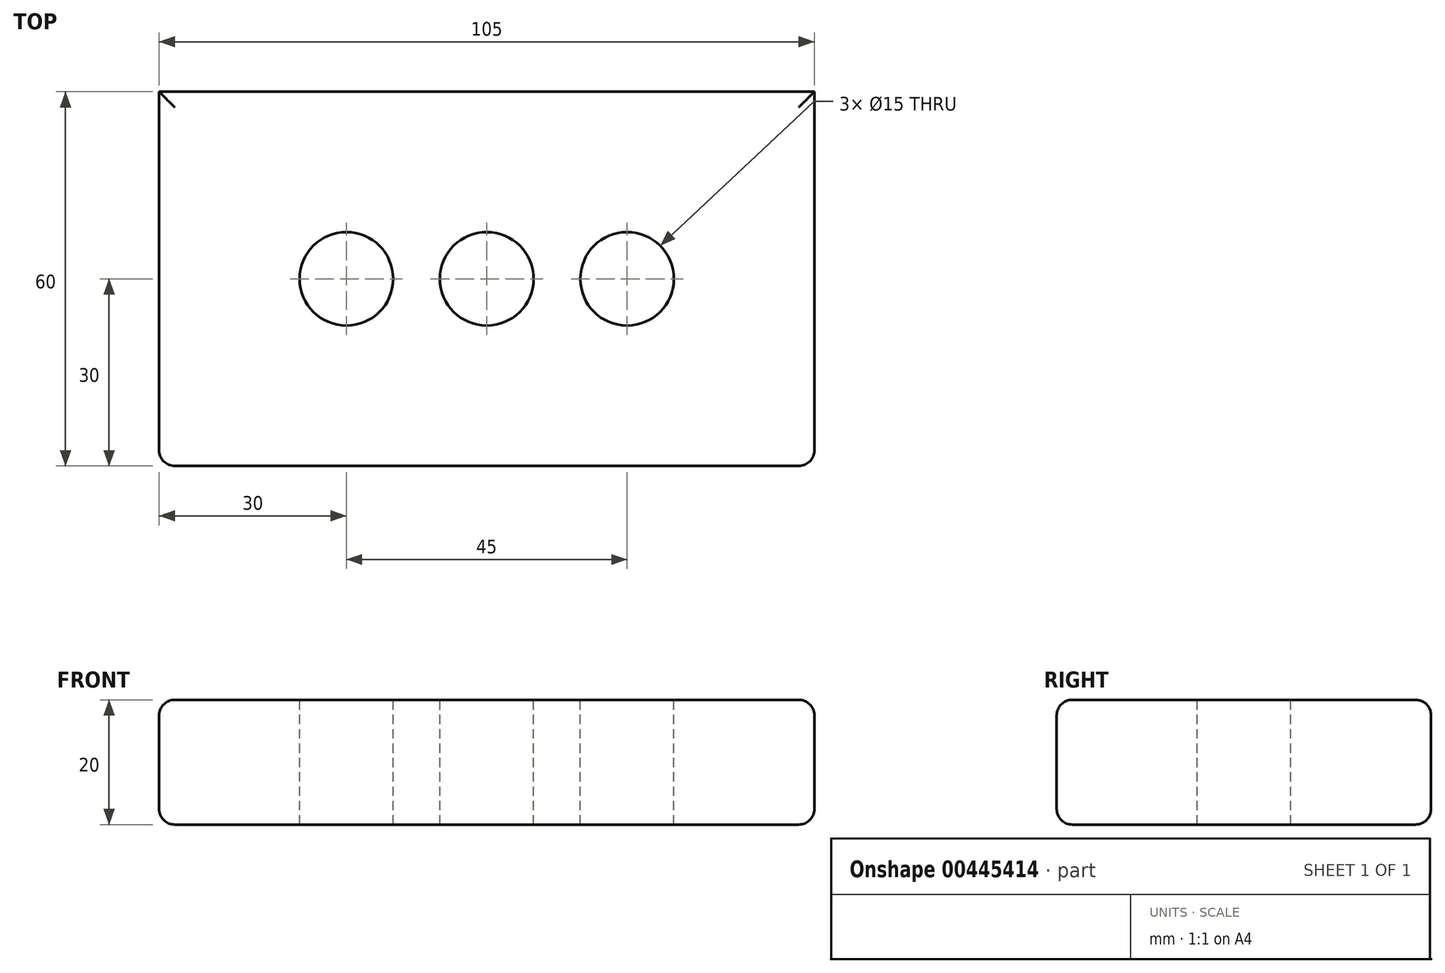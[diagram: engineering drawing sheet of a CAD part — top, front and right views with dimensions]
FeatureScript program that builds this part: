
annotation { "Feature Type Name" : "Feature", "Feature Type Description" : "" }
export const myFeature = defineFeature(function(context is Context, id is Id, definition is map)
    precondition{}
    {
        {
            var Q0;
            Q0=qCreatedBy(makeId("Top.planeOp"),FACE);
            var sketch = newSketch(context, id + "F0", { "sketchPlane" : qUnion([Q0])});
            skLineSegment(sketch, "E0.bottom", {"start": v(52.5, 30) * mm, "end": v(-52.5, 30) * mm});
            skLineSegment(sketch, "E0.top", {"start": v(52.5, -30) * mm, "end": v(-52.5, -30) * mm});
            skLineSegment(sketch, "E0.left", {"start": v(52.5, 30) * mm, "end": v(52.5, -30) * mm});
            skLineSegment(sketch, "E0.right", {"start": v(-52.5, 30) * mm, "end": v(-52.5, -30) * mm});
            skPoint(sketch, "E0.middle", {"position": v(0, 0) * mm});
            skSolve(sketch);
        }
        {
            var Q0;
            Q0 = qSketchRegion(id + "F0", true);
            extrude(context, id + "F1", {"entities" : qUnion([Q0]), "oppositeDirection" : true, "depth" : 20 * mm});
        }
        {
            var Q0;
            Q0=makeQuery(id+"F1.opExtrude","CAP_FACE",FACE,{"disambiguationData":[OSD([sQuery(id+"F0.wireOp",EDGE,"E0.bottom"),sQuery(id+"F0.wireOp",EDGE,"E0.top"),sQuery(id+"F0.wireOp",EDGE,"E0.left"),sQuery(id+"F0.wireOp",EDGE,"E0.right")])],"isStart":true});
            var sketch = newSketch(context, id + "F2", { "sketchPlane" : qUnion([Q0])});
            skCircle(sketch, "E1", {"center": v(0, 0) * mm, "radius": 7.5 * mm});
            skLineSegment(sketch, "E2", {"start": v(-7.5, 0) * mm, "end": v(-22.5, 0) * mm});
            skLineSegment(sketch, "E3", {"start": v(7.5, 0) * mm, "end": v(22.5, 0) * mm});
            skCircle(sketch, "E4", {"center": v(-22.5, 0) * mm, "radius": 7.5 * mm});
            skCircle(sketch, "E5", {"center": v(22.5, 0) * mm, "radius": 7.5 * mm});
            skSolve(sketch);
        }
        {
            var Q0;
            Q0 = qSketchRegion(id + "F2", true);
            extrude(context, id + "F3", {"entities" : qUnion([Q0]), "operationType" : NewBodyOperationType.REMOVE, "oppositeDirection" : true, "depth" : 68.6 * mm});
        }
        {
            var Q0;
            Q0 = qSketchRegion(id + "F2", true);
            extrude(context, id + "F4", {"entities" : qUnion([Q0]), "operationType" : NewBodyOperationType.REMOVE, "oppositeDirection" : true, "depth" : 55.5 * mm});
        }
        {
            var Q0;
            Q0=makeQuery(id+"F1.opExtrude","CAP_EDGE",EDGE,{"disambiguationData":[OSD([sQuery(id+"F0.wireOp",EDGE,"E0.top")])],"isStart":true});
            var Q1;
            Q1=makeQuery(id+"F1.opExtrude","CAP_EDGE",EDGE,{"disambiguationData":[OSD([sQuery(id+"F0.wireOp",EDGE,"E0.left")])],"isStart":true});
            var Q2;
            Q2=makeQuery(id+"F1.opExtrude","CAP_EDGE",EDGE,{"disambiguationData":[OSD([sQuery(id+"F0.wireOp",EDGE,"E0.left")])],"isStart":false});
            var Q3;
            Q3=makeQuery(id+"F1.opExtrude","SWEPT_EDGE",EDGE,{"disambiguationData":[OSD([sQuery(id+"F0.wireOp",EDGE,"E0.top"),sQuery(id+"F0.wireOp",EDGE,"E0.left")])]});
            var Q4;
            Q4=makeQuery(id+"F1.opExtrude","CAP_EDGE",EDGE,{"disambiguationData":[OSD([sQuery(id+"F0.wireOp",EDGE,"E0.top")])],"isStart":false});
            var Q5;
            Q5=makeQuery(id+"F1.opExtrude","SWEPT_EDGE",EDGE,{"disambiguationData":[OSD([sQuery(id+"F0.wireOp",EDGE,"E0.top"),sQuery(id+"F0.wireOp",EDGE,"E0.right")])]});
            var Q6;
            Q6=makeQuery(id+"F1.opExtrude","CAP_EDGE",EDGE,{"disambiguationData":[OSD([sQuery(id+"F0.wireOp",EDGE,"E0.right")])],"isStart":true});
            var Q7;
            Q7=makeQuery(id+"F1.opExtrude","CAP_EDGE",EDGE,{"disambiguationData":[OSD([sQuery(id+"F0.wireOp",EDGE,"E0.right")])],"isStart":false});
            var Q8;
            Q8=makeQuery(id+"F1.opExtrude","CAP_EDGE",EDGE,{"disambiguationData":[OSD([sQuery(id+"F0.wireOp",EDGE,"E0.bottom")])],"isStart":true});
            var Q9;
            Q9=makeQuery(id+"F1.opExtrude","CAP_EDGE",EDGE,{"disambiguationData":[OSD([sQuery(id+"F0.wireOp",EDGE,"E0.bottom")])],"isStart":false});
            fillet(context, id + "F5", {"entities" : qUnion([Q0, Q1, Q2, Q3, Q4, Q5, Q6, Q7, Q8, Q9]), "radius" : 2.5 * mm, "tangentPropagation" : true, "allowEdgeOverflow" : false});
        }
    });
